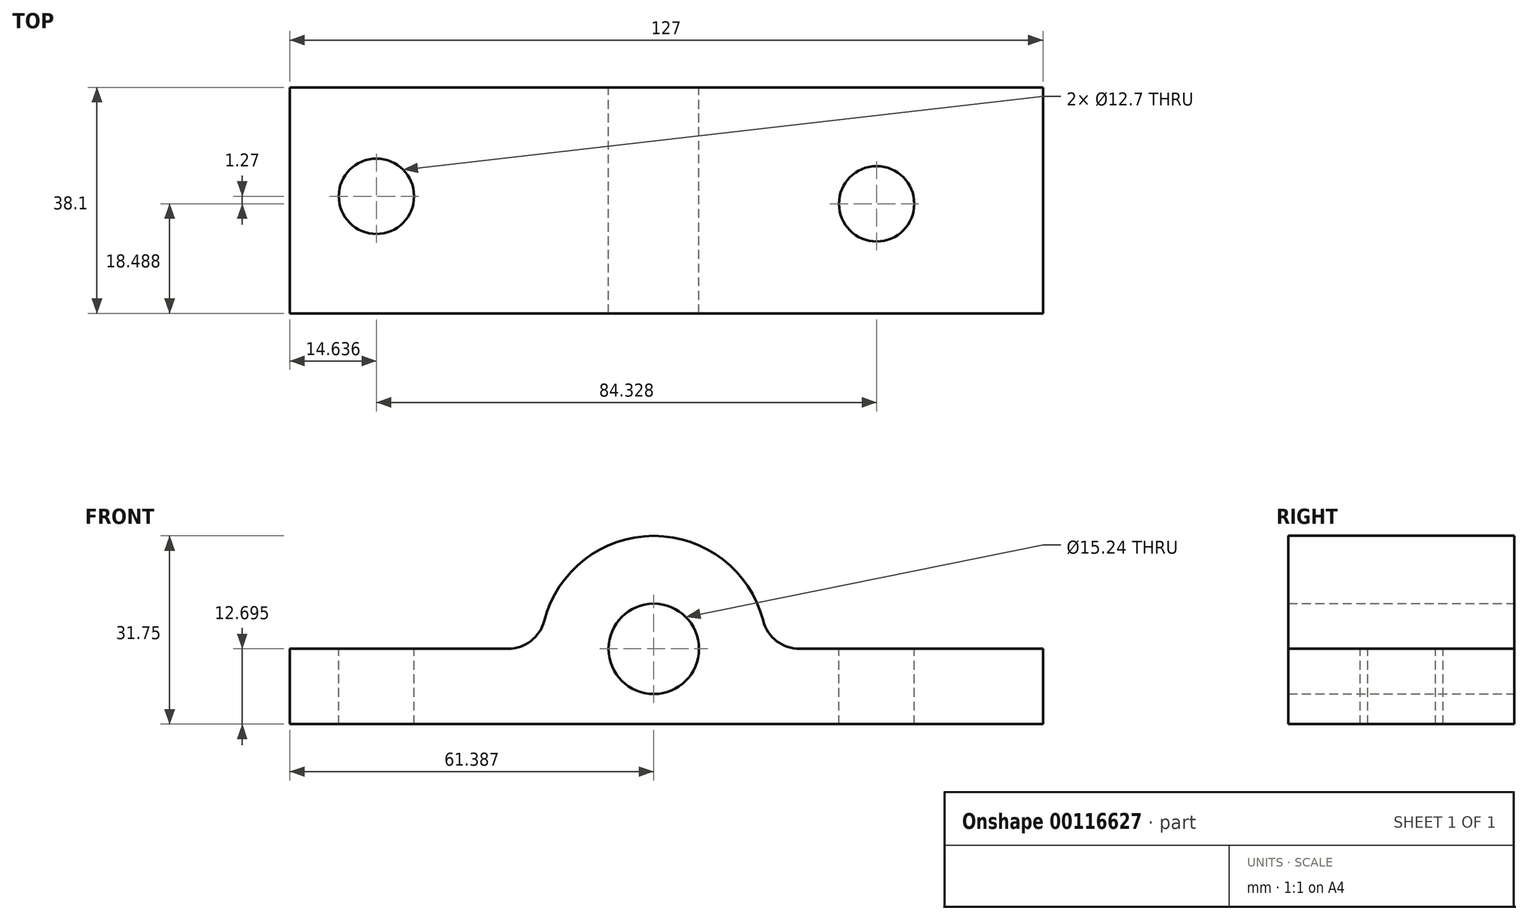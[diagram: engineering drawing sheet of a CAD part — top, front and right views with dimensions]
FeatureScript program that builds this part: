
annotation { "Feature Type Name" : "Feature", "Feature Type Description" : "" }
export const myFeature = defineFeature(function(context is Context, id is Id, definition is map)
    precondition{}
    {
        {
            var Q0;
            Q0=qCreatedBy(makeId("Front.planeOp"),FACE);
            var sketch = newSketch(context, id + "F0", { "sketchPlane" : qUnion([Q0])});
            skLineSegment(sketch, "E0", {"start": v(62.98, -28.26) * mm, "end": v(-64.02, -28.26) * mm});
            skLineSegment(sketch, "E1", {"start": v(-64.02, -28.26) * mm, "end": v(-64.02, -15.56) * mm});
            skLineSegment(sketch, "E2", {"start": v(-64.02, -15.56) * mm, "end": v(-27.23, -15.56) * mm});
            skArc(sketch, "E3", {"start": v(15.81, -10.8) * mm, "mid": v(-2.63, 3.49) * mm, "end": v(-21.08, -10.8) * mm});
            skLineSegment(sketch, "E4", {"start": v(21.96, -15.56) * mm, "end": v(62.98, -15.56) * mm});
            skLineSegment(sketch, "E5", {"start": v(62.98, -15.56) * mm, "end": v(62.98, -28.26) * mm});
            skCircle(sketch, "E6", {"center": v(-2.63, -15.56) * mm, "radius": 7.62 * mm});
            skPoint(sketch, "E7.visualSharp", {"position": v(-21.68, -15.56) * mm});
            skArc(sketch, "E7.filletArc", {"start": v(-27.23, -15.56) * mm, "mid": v(-23.34, -14.23) * mm, "end": v(-21.08, -10.8) * mm});
            skPoint(sketch, "E8.visualSharp", {"position": v(16.42, -15.56) * mm});
            skArc(sketch, "E8.filletArc", {"start": v(15.81, -10.8) * mm, "mid": v(18.07, -14.23) * mm, "end": v(21.96, -15.56) * mm});
            skSolve(sketch);
        }
        {
            var Q0;
            Q0=makeQuery(id+"F0.imprint","IMPRINT",FACE,{"disambiguationData":[TD([[makeQuery(id+"F0.imprint","IMPRINT",EDGE,{"derivedFrom":sQuery(id+"F0.wireOp",EDGE,"E0")}),-1.0]])]});
            extrude(context, id + "F1", {"entities" : qUnion([Q0]), "depth" : 38.1 * mm});
        }
        {
            var Q0;
            Q0=makeQuery(id+"F1.opExtrude","SWEPT_FACE",FACE,{"disambiguationData":[OSD([sQuery(id+"F0.wireOp",EDGE,"E2")])]});
            var sketch = newSketch(context, id + "F2", { "sketchPlane" : qUnion([Q0])});
            skCircle(sketch, "E9", {"center": v(-49.38, -18.34) * mm, "radius": 6.35 * mm});
            skCircle(sketch, "E10", {"center": v(34.94, -19.61) * mm, "radius": 6.35 * mm});
            skSolve(sketch);
        }
        {
            var Q0;
            Q0=makeQuery(id+"F2.imprint","IMPRINT",FACE,{"disambiguationData":[TD([[makeQuery(id+"F2.imprint","IMPRINT",EDGE,{"derivedFrom":sQuery(id+"F2.wireOp",EDGE,"E9")}),1.0]])]});
            var Q1;
            Q1=makeQuery(id+"F2.imprint","IMPRINT",FACE,{"disambiguationData":[TD([[makeQuery(id+"F2.imprint","IMPRINT",EDGE,{"derivedFrom":sQuery(id+"F2.wireOp",EDGE,"E10")}),1.0]])]});
            extrude(context, id + "F3", {"entities" : qUnion([Q0, Q1]), "operationType" : NewBodyOperationType.REMOVE, "oppositeDirection" : true, "depth" : 25.4 * mm});
        }
    });
